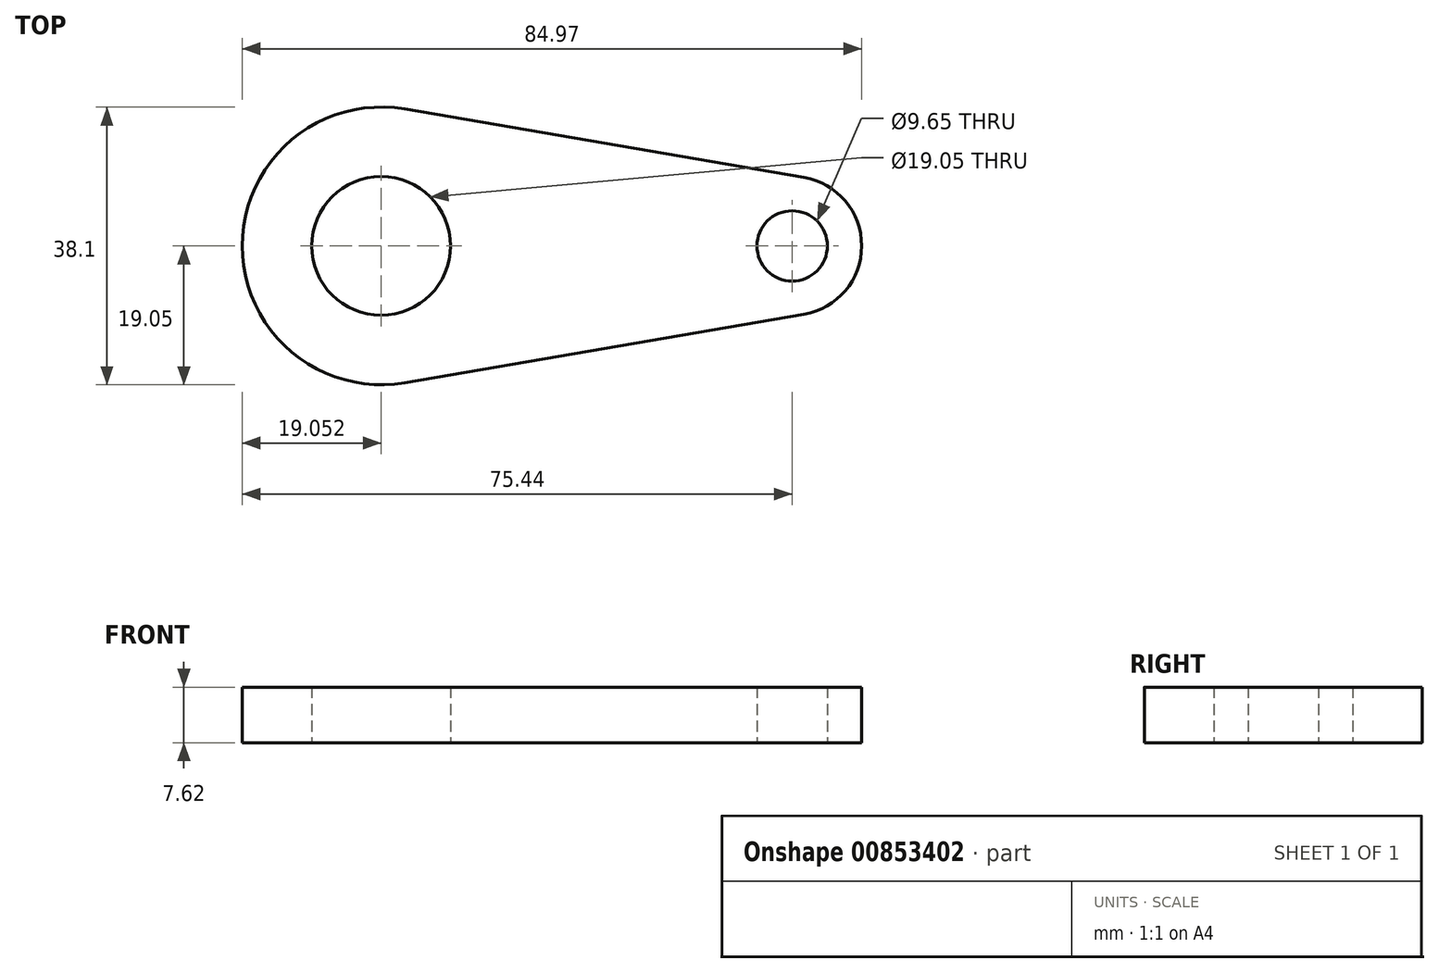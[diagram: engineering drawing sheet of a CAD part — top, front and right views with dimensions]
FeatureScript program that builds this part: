
annotation { "Feature Type Name" : "Feature", "Feature Type Description" : "" }
export const myFeature = defineFeature(function(context is Context, id is Id, definition is map)
    precondition{}
    {
        {
            var Q0;
            Q0=qCreatedBy(makeId("Top.planeOp"),FACE);
            var sketch = newSketch(context, id + "F0", { "sketchPlane" : qUnion([Q0])});
            skArc(sketch, "E0", {"start": v(1.6, -9.39) * mm, "mid": v(9.53, 0) * mm, "end": v(1.6, 9.39) * mm});
            skCircle(sketch, "E1", {"center": v(0, 0) * mm, "radius": 4.83 * mm});
            skArc(sketch, "E2", {"start": v(-53.17, 18.78) * mm, "mid": v(-75.44, 0) * mm, "end": v(-53.17, -18.78) * mm});
            skCircle(sketch, "E3", {"center": v(-56.39, 0) * mm, "radius": 9.53 * mm});
            skLineSegment(sketch, "E4", {"start": v(-89.63, 0) * mm, "end": v(45.69, 0) * mm, "construction": true});
            skLineSegment(sketch, "E5", {"start": v(-53.17, 18.78) * mm, "end": v(1.6, 9.39) * mm});
            skLineSegment(sketch, "E6.MirrorCS", {"start": v(-53.17, -18.78) * mm, "end": v(1.6, -9.39) * mm});
            skSolve(sketch);
        }
        {
            var Q0;
            Q0 = qSketchRegion(id + "F0", true);
            extrude(context, id + "F1", {"entities" : qUnion([Q0]), "depth" : 7.62 * mm, "offsetDistance" : 25.4 * mm});
        }
    });
